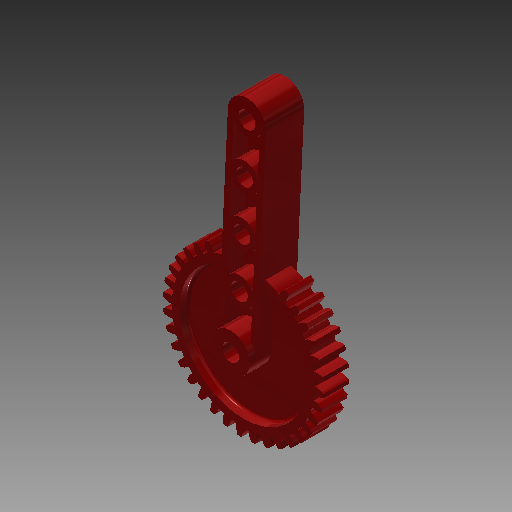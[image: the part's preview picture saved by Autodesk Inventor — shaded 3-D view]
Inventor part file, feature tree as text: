
AUTODESK INVENTOR PART (.ipt)
format: ipt  version: 2018 (Build 220112000, 112)  size: 1,575,424 bytes
history: native  units: mm (DEFAULTED — no unit token found)
features: plane x2, imported_body x1
ambient origin geometry x8: Origin, YZ Plane, XZ Plane, XY Plane, X Axis, Y Axis, Z Axis, Center Point
bodies: Solid1 (feature_tree)
feature tree (3):
  imported_body  "Base1"
  plane  "Work Plane1"
  plane  "Work Plane2"
